# Revit family: Kosz_nascienny_na_odpadki_higieniczne 7 l stal szlachetna matowa
name_source: partatom
category: Furniture
units: mm (PartAtom-declared; Revit-internal decimal feet)

## family parameters
Always vertical = Yes
Cut with Voids When Loaded = No
Host = Wall
Room Calculation Point = No
Shared = No

## types (1)
- WB7SJB
    Depth / Glebokosc = 107 mm  [stored 0.35105 ft]
    Description = Kosz naścienny na odpadki higieniczne o pojemności 7 l został wykonany z odpornej na uszkodzenia stali nierdzewnej. Jest to model łatwy w obsłudze i czyszczeniu, gwarantujący wysoki poziom higieny. Matowe wykończenie nadaje mu nowoczesny wygląd, a naścienny montaż podnosi funkcjonalność i wygodę użytkowania. Ten model pojemnika na odpady idealnie sprawdzi się we wszystkich toaletach publicznych, a szczególnie polecany jest do damskich.
    Height / Wysokosc = 285 mm  [stored 0.935039 ft]
    Manufacturer = FANECO.com
    Manufacturer code / Kod producenta = 5901764293422
    Material = Stal nierdzewna szczotkowana
    Material finish / Wykonczenie = Stal nierdzewna 430 szczotkowana, mat.
    Product code / Kod produktu = WB7SJB
    Type Comments = Kosz naścienny na odpadki higieniczne 7 l stal szlachetna matowa
    URL = https://faneco.com
    Weight / Waga = 1.7 kg
    Width / Szerokosc = 234 mm  [stored 0.767717 ft]

note: [stored X ft] marks values corroborated as IEEE doubles in the binary element streams (Revit-internal decimal feet)

## geometry (parser evidence)
native form markers: Sweep x11
no freeform markers — native parametric forms only
